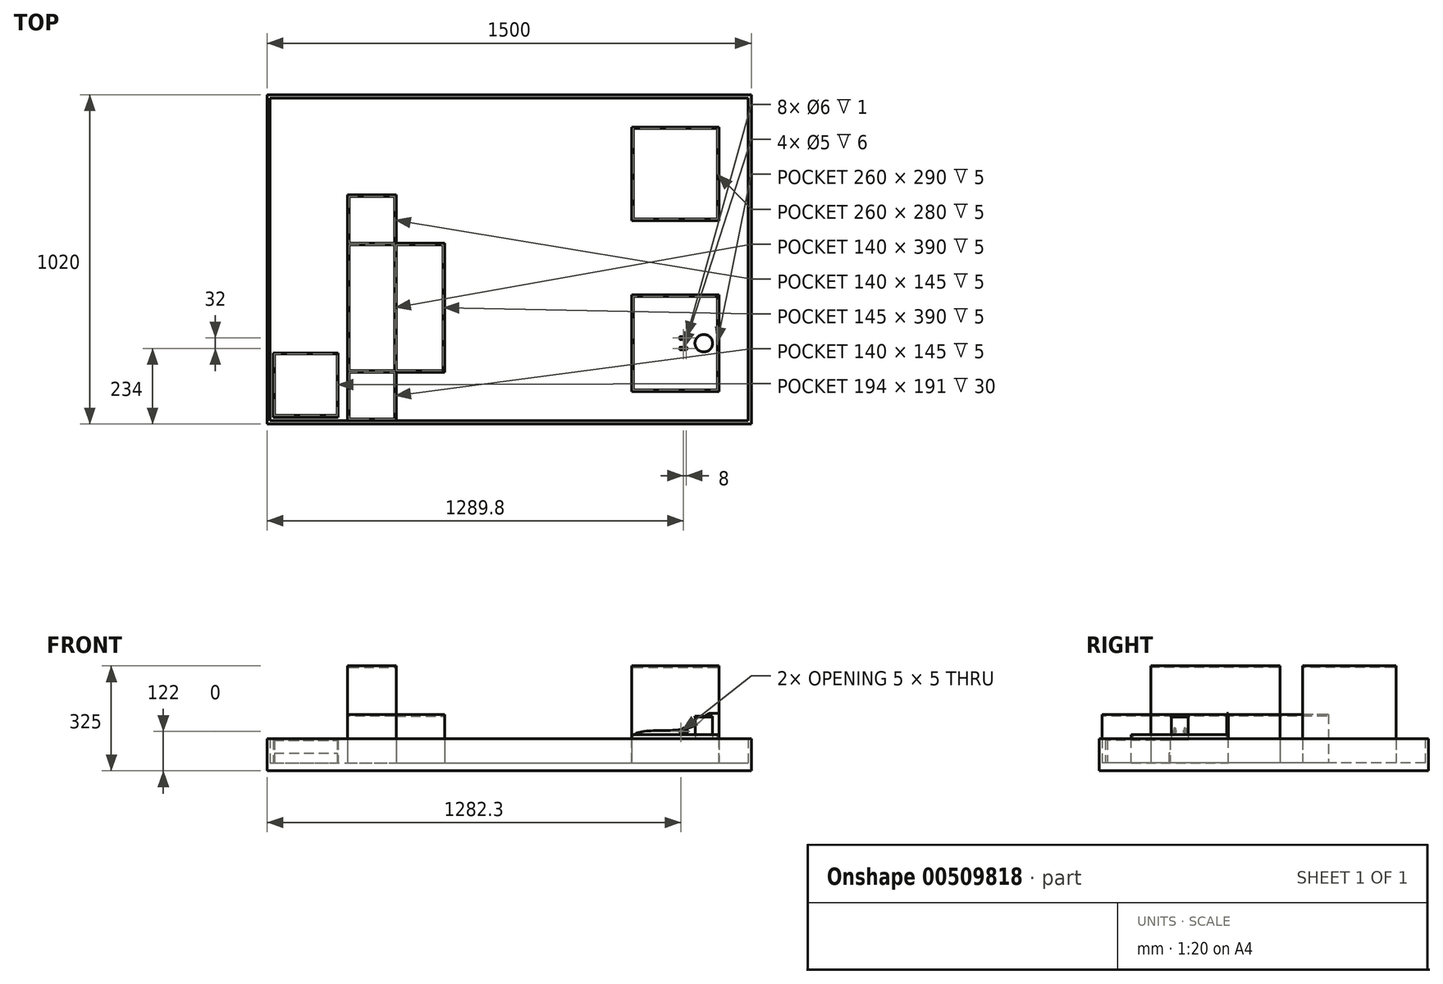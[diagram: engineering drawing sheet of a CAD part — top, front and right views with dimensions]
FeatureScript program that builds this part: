
annotation { "Feature Type Name" : "Feature", "Feature Type Description" : "" }
export const myFeature = defineFeature(function(context is Context, id is Id, definition is map)
    precondition{}
    {
        {
            var Q0;
            Q0=qCreatedBy(makeId("Top.planeOp"),FACE);
            var sketch = newSketch(context, id + "F0", { "sketchPlane" : qUnion([Q0])});
            skCircle(sketch, "E0", {"center": v(0, 0) * mm, "radius": 27.2 * mm});
            skSolve(sketch);
        }
        {
            var Q0;
            Q0=qSketchRegion(id+"F0",true);
            extrude(context, id + "F1", {"entities" : qUnion([Q0]), "depth" : 2.83 * mm});
        }
        {
            var Q0;
            Q0=makeQuery(id+"F1.opExtrude","CAP_FACE",FACE,{"disambiguationData":[OSD([sQuery(id+"F0.wireOp",EDGE,"E0")])],"isStart":false});
            var sketch = newSketch(context, id + "F2", { "sketchPlane" : qUnion([Q0])});
            skCircle(sketch, "E1", {"center": v(0, 0) * mm, "radius": 26.4 * mm});
            skSolve(sketch);
        }
        {
            var Q0;
            Q0=qSketchRegion(id+"F2",true);
            extrude(context, id + "F3", {"entities" : qUnion([Q0]), "operationType" : NewBodyOperationType.ADD, "depth" : 67.36 * mm});
        }
        {
            var Q0;
            Q0=makeQuery(id+"F3.opExtrude","CAP_FACE",FACE,{"disambiguationData":[OSD([sQuery(id+"F2.wireOp",EDGE,"E1")])],"isStart":false});
            var sketch = newSketch(context, id + "F4", { "sketchPlane" : qUnion([Q0])});
            skCircle(sketch, "E2", {"center": v(0, 0) * mm, "radius": 27.2 * mm});
            skSolve(sketch);
        }
        {
            var Q0;
            Q0=qSketchRegion(id+"F4",true);
            extrude(context, id + "F5", {"entities" : qUnion([Q0]), "operationType" : NewBodyOperationType.ADD, "depth" : 2.83 * mm});
        }
        {
            var Q0;
            Q0=makeQuery(id+"F5.opExtrude","CAP_FACE",FACE,{"disambiguationData":[OSD([sQuery(id+"F4.wireOp",EDGE,"E2")])],"isStart":false});
            var sketch = newSketch(context, id + "F6", { "sketchPlane" : qUnion([Q0])});
            skSolve(sketch);
        }
        {
            var Q0;
            Q0=qCreatedBy(makeId("Top.planeOp"),FACE);
            cPlane(context, id + "F7", {"entities" : qUnion([Q0]), "cplaneType" : CPlaneType.OFFSET, "offset" : 25 * mm, "width" : 150 * mm, "height" : 150 * mm});
        }
        {
            var Q0;
            Q0=makeQuery(id+"F6.imprint","IMPRINT",FACE,{"disambiguationData":[TD([[makeQuery(id+"F6.imprint","IMPRINT",EDGE,{"derivedFrom":makeQuery(id+"F5.opExtrude","CAP_EDGE",EDGE,{"disambiguationData":[OSD([sQuery(id+"F4.wireOp",EDGE,"E2")])],"isStart":false})}),1.0]])]});
            var sketch = newSketch(context, id + "F8", { "sketchPlane" : qUnion([Q0])});
            skSolve(sketch);
        }
        {
            var Q0;
            Q0=qCreatedBy(makeId("Top.planeOp"),FACE);
            var sketch = newSketch(context, id + "F9", { "sketchPlane" : qUnion([Q0])});
            skLineSegment(sketch, "E3.bottom", {"start": v(-222.8, -150) * mm, "end": v(47.2, -150) * mm});
            skLineSegment(sketch, "E3.top", {"start": v(-222.8, 150) * mm, "end": v(47.2, 150) * mm});
            skLineSegment(sketch, "E3.left", {"start": v(-222.8, -150) * mm, "end": v(-222.8, 150) * mm});
            skLineSegment(sketch, "E3.right", {"start": v(47.2, -150) * mm, "end": v(47.2, 150) * mm});
            skSolve(sketch);
        }
        {
            var Q0;
            Q0=qSketchRegion(id+"F9",true);
            extrude(context, id + "F10", {"entities" : qUnion([Q0]), "oppositeDirection" : true, "depth" : 72 * mm});
        }
        {
            var Q0;
            Q0=makeQuery(id+"F10.opExtrude","CAP_FACE",FACE,{"disambiguationData":[OSD([sQuery(id+"F9.wireOp",EDGE,"E3.bottom"),sQuery(id+"F9.wireOp",EDGE,"E3.top"),sQuery(id+"F9.wireOp",EDGE,"E3.left"),sQuery(id+"F9.wireOp",EDGE,"E3.right")])],"isStart":true});
            var sketch = newSketch(context, id + "F11", { "sketchPlane" : qUnion([Q0])});
            skLineSegment(sketch, "E4.bottom", {"start": v(-222.8, -150) * mm, "end": v(47.2, -150) * mm});
            skLineSegment(sketch, "E4.top", {"start": v(-222.8, -145) * mm, "end": v(42.2, -145) * mm});
            skLineSegment(sketch, "E4.left", {"start": v(-222.8, -150) * mm, "end": v(-222.8, -145) * mm});
            skLineSegment(sketch, "E5.bottom", {"start": v(47.2, 150) * mm, "end": v(42.2, 150) * mm});
            skLineSegment(sketch, "E5.left", {"start": v(47.2, 150) * mm, "end": v(47.2, -150) * mm});
            skLineSegment(sketch, "E5.right", {"start": v(42.2, 150) * mm, "end": v(42.2, -145) * mm});
            skSolve(sketch);
        }
        {
            var Q0;
            Q0=qSketchRegion(id+"F11",true);
            extrude(context, id + "F12", {"entities" : qUnion([Q0]), "operationType" : NewBodyOperationType.ADD, "depth" : 15 * mm});
        }
        {
            var Q0;
            Q0=makeQuery(id+"F12.boolean.opBoolean","MERGE",FACE,{"derivedFrom":[makeQuery(id+"F10.opExtrude","SWEPT_FACE",FACE,{"disambiguationData":[OSD([sQuery(id+"F9.wireOp",EDGE,"E3.top")])]}),makeQuery(id+"F12.opExtrude","SWEPT_FACE",FACE,{"disambiguationData":[OSD([sQuery(id+"F11.wireOp",EDGE,"E5.bottom")])]})]});
            var sketch = newSketch(context, id + "F13", { "sketchPlane" : qUnion([Q0])});
            skLineSegment(sketch, "E6", {"start": v(-47.2, 81.36) * mm, "end": v(-21.31, 81.36) * mm});
            skFitSpline(sketch, "E7", {"points": [v(-21.31, 81.36) * mm, v(15.24, 52.01) * mm, v(114.14, 28.17) * mm, v(222.8, 0) * mm], "startDerivative": vector(181.02, 0.3) * mm, "endDerivative": vector(-1.73, -239.85) * mm});
            skLineSegment(sketch, "E8", {"start": v(-47.2, 81.36) * mm, "end": v(-47.2, -72) * mm});
            skLineSegment(sketch, "E9", {"start": v(-47.2, -72) * mm, "end": v(222.8, -72) * mm});
            skLineSegment(sketch, "E10", {"start": v(222.8, -72) * mm, "end": v(222.8, 0) * mm});
            skSolve(sketch);
        }
        {
            var Q0;
            Q0=qSketchRegion(id+"F13",true);
            extrude(context, id + "F14", {"entities" : qUnion([Q0]), "operationType" : NewBodyOperationType.ADD, "oppositeDirection" : true, "depth" : 5 * mm});
        }
        {
            var Q0;
            Q0=makeQuery(id+"F10.opExtrude","CAP_FACE",FACE,{"disambiguationData":[OSD([sQuery(id+"F9.wireOp",EDGE,"E3.bottom"),sQuery(id+"F9.wireOp",EDGE,"E3.top"),sQuery(id+"F9.wireOp",EDGE,"E3.left"),sQuery(id+"F9.wireOp",EDGE,"E3.right")])],"isStart":true});
            var sketch = newSketch(context, id + "F15", { "sketchPlane" : qUnion([Q0])});
            skLineSegment(sketch, "E11.bottom", {"start": v(-222.8, 145) * mm, "end": v(-217.8, 145) * mm});
            skLineSegment(sketch, "E11.top", {"start": v(-222.8, -145) * mm, "end": v(-217.8, -145) * mm});
            skLineSegment(sketch, "E11.left", {"start": v(-222.8, 145) * mm, "end": v(-222.8, -145) * mm});
            skLineSegment(sketch, "E11.right", {"start": v(-217.8, 145) * mm, "end": v(-217.8, -145) * mm});
            skSolve(sketch);
        }
        {
            var Q0;
            Q0=qSketchRegion(id+"F15",true);
            extrude(context, id + "F16", {"entities" : qUnion([Q0]), "operationType" : NewBodyOperationType.ADD, "depth" : 5 * mm});
        }
        {
            var Q0;
            Q0=makeQuery(id+"F10.opExtrude","CAP_FACE",FACE,{"disambiguationData":[OSD([sQuery(id+"F9.wireOp",EDGE,"E3.bottom"),sQuery(id+"F9.wireOp",EDGE,"E3.top"),sQuery(id+"F9.wireOp",EDGE,"E3.left"),sQuery(id+"F9.wireOp",EDGE,"E3.right")])],"isStart":false});
            var sketch = newSketch(context, id + "F17", { "sketchPlane" : qUnion([Q0])});
            skLineSegment(sketch, "E12.bottom", {"start": v(147.2, 250) * mm, "end": v(-1352.8, 250) * mm});
            skLineSegment(sketch, "E12.top", {"start": v(147.2, -770) * mm, "end": v(-1352.8, -770) * mm});
            skLineSegment(sketch, "E12.left", {"start": v(147.2, 250) * mm, "end": v(147.2, -770) * mm});
            skLineSegment(sketch, "E12.right", {"start": v(-1352.8, 250) * mm, "end": v(-1352.8, -770) * mm});
            skSolve(sketch);
        }
        {
            var Q0;
            Q0=qSketchRegion(id+"F17",true);
            extrude(context, id + "F18", {"entities" : qUnion([Q0]), "operationType" : NewBodyOperationType.ADD, "depth" : 25 * mm});
        }
        {
            var Q0;
            Q0=makeQuery(id+"F18.opExtrude","CAP_FACE",FACE,{"disambiguationData":[OSD([sQuery(id+"F17.wireOp",EDGE,"E12.bottom"),sQuery(id+"F17.wireOp",EDGE,"E12.top"),sQuery(id+"F17.wireOp",EDGE,"E12.left"),sQuery(id+"F17.wireOp",EDGE,"E12.right")])],"isStart":true});
            var sketch = newSketch(context, id + "F19", { "sketchPlane" : qUnion([Q0])});
            skLineSegment(sketch, "E13.bottom", {"start": v(-222.8, 670) * mm, "end": v(47.2, 670) * mm});
            skLineSegment(sketch, "E13.top", {"start": v(-222.8, 380) * mm, "end": v(47.2, 380) * mm});
            skLineSegment(sketch, "E13.left", {"start": v(-222.8, 670) * mm, "end": v(-222.8, 380) * mm});
            skLineSegment(sketch, "E13.right", {"start": v(47.2, 670) * mm, "end": v(47.2, 380) * mm});
            skSolve(sketch);
        }
        {
            var Q0;
            Q0=qSketchRegion(id+"F19",true);
            extrude(context, id + "F20", {"entities" : qUnion([Q0]), "operationType" : NewBodyOperationType.ADD, "depth" : 300 * mm});
        }
        {
            var Q0;
            Q0=makeQuery(id+"F20.opExtrude","CAP_FACE",FACE,{"disambiguationData":[OSD([sQuery(id+"F19.wireOp",EDGE,"E13.bottom"),sQuery(id+"F19.wireOp",EDGE,"E13.top"),sQuery(id+"F19.wireOp",EDGE,"E13.left"),sQuery(id+"F19.wireOp",EDGE,"E13.right")])],"isStart":false});
            var sketch = newSketch(context, id + "F21", { "sketchPlane" : qUnion([Q0])});
            skLineSegment(sketch, "E14.bottom", {"start": v(-217.8, 665) * mm, "end": v(42.2, 665) * mm});
            skLineSegment(sketch, "E14.top", {"start": v(-217.8, 385) * mm, "end": v(42.2, 385) * mm});
            skLineSegment(sketch, "E14.left", {"start": v(-217.8, 665) * mm, "end": v(-217.8, 385) * mm});
            skLineSegment(sketch, "E14.right", {"start": v(42.2, 665) * mm, "end": v(42.2, 385) * mm});
            skSolve(sketch);
        }
        {
            var Q0;
            Q0=qSketchRegion(id+"F21",true);
            extrude(context, id + "F22", {"entities" : qUnion([Q0]), "operationType" : NewBodyOperationType.REMOVE, "oppositeDirection" : true, "depth" : 5 * mm});
        }
        {
            var Q0;
            Q0=makeQuery(id+"F18.opExtrude","CAP_FACE",FACE,{"disambiguationData":[OSD([sQuery(id+"F17.wireOp",EDGE,"E12.bottom"),sQuery(id+"F17.wireOp",EDGE,"E12.top"),sQuery(id+"F17.wireOp",EDGE,"E12.left"),sQuery(id+"F17.wireOp",EDGE,"E12.right")])],"isStart":true});
            var sketch = newSketch(context, id + "F23", { "sketchPlane" : qUnion([Q0])});
            skLineSegment(sketch, "E15.bottom", {"start": v(-1352.8, 770) * mm, "end": v(147.2, 770) * mm});
            skLineSegment(sketch, "E15.top", {"start": v(-1352.8, -250) * mm, "end": v(147.2, -250) * mm});
            skLineSegment(sketch, "E15.left", {"start": v(-1352.8, 770) * mm, "end": v(-1352.8, -250) * mm});
            skLineSegment(sketch, "E15.right", {"start": v(147.2, 770) * mm, "end": v(147.2, -250) * mm});
            skLineSegment(sketch, "E16.bottom", {"start": v(-1342.8, 760) * mm, "end": v(137.2, 760) * mm});
            skLineSegment(sketch, "E16.top", {"start": v(-1342.8, -240) * mm, "end": v(137.2, -240) * mm});
            skLineSegment(sketch, "E16.left", {"start": v(-1342.8, 760) * mm, "end": v(-1342.8, -240) * mm});
            skLineSegment(sketch, "E16.right", {"start": v(137.2, 760) * mm, "end": v(137.2, -240) * mm});
            skSolve(sketch);
        }
        {
            var Q0;
            Q0=qSketchRegion(id+"F23",true);
            extrude(context, id + "F24", {"entities" : qUnion([Q0]), "operationType" : NewBodyOperationType.ADD, "depth" : 75 * mm});
        }
        {
            var Q0;
            Q0=makeQuery(id+"F18.opExtrude","CAP_FACE",FACE,{"disambiguationData":[OSD([sQuery(id+"F17.wireOp",EDGE,"E12.bottom"),sQuery(id+"F17.wireOp",EDGE,"E12.top"),sQuery(id+"F17.wireOp",EDGE,"E12.left"),sQuery(id+"F17.wireOp",EDGE,"E12.right")])],"isStart":true});
            var sketch = newSketch(context, id + "F25", { "sketchPlane" : qUnion([Q0])});
            skLineSegment(sketch, "E17.bottom", {"start": v(-1102.8, 460) * mm, "end": v(-952.8, 460) * mm});
            skLineSegment(sketch, "E17.top", {"start": v(-1102.8, -240) * mm, "end": v(-952.8, -240) * mm});
            skLineSegment(sketch, "E17.left", {"start": v(-1102.8, 460) * mm, "end": v(-1102.8, -240) * mm});
            skLineSegment(sketch, "E17.right", {"start": v(-952.8, 460) * mm, "end": v(-952.8, 310) * mm});
            skLineSegment(sketch, "E18.bottom", {"start": v(-952.8, 310) * mm, "end": v(-802.8, 310) * mm});
            skLineSegment(sketch, "E18.top", {"start": v(-952.8, -90) * mm, "end": v(-802.8, -90) * mm});
            skLineSegment(sketch, "E18.right", {"start": v(-802.8, 310) * mm, "end": v(-802.8, -90) * mm});
            skLineSegment(sketch, "E19.trimOffspring", {"start": v(-952.8, -90) * mm, "end": v(-952.8, -240) * mm});
            skSolve(sketch);
        }
        {
            var Q0;
            Q0=qSketchRegion(id+"F25",true);
            extrude(context, id + "F26", {"entities" : qUnion([Q0]), "operationType" : NewBodyOperationType.ADD, "depth" : 150 * mm});
        }
        {
            var Q0;
            Q0=makeQuery(id+"F26.opExtrude","CAP_FACE",FACE,{"disambiguationData":[OSD([sQuery(id+"F25.wireOp",EDGE,"E17.bottom"),sQuery(id+"F25.wireOp",EDGE,"E17.top"),sQuery(id+"F25.wireOp",EDGE,"E17.left"),sQuery(id+"F25.wireOp",EDGE,"E17.right"),sQuery(id+"F25.wireOp",EDGE,"E18.bottom"),sQuery(id+"F25.wireOp",EDGE,"E18.top"),sQuery(id+"F25.wireOp",EDGE,"E18.right"),sQuery(id+"F25.wireOp",EDGE,"E19.trimOffspring")])],"isStart":false});
            var sketch = newSketch(context, id + "F27", { "sketchPlane" : qUnion([Q0])});
            skLineSegment(sketch, "E20.bottom", {"start": v(-952.8, 310) * mm, "end": v(-1102.8, 310) * mm});
            skLineSegment(sketch, "E20.top", {"start": v(-952.8, -90) * mm, "end": v(-1102.8, -90) * mm});
            skLineSegment(sketch, "E20.left", {"start": v(-952.8, 310) * mm, "end": v(-952.8, -90) * mm});
            skLineSegment(sketch, "E20.right", {"start": v(-1102.8, 310) * mm, "end": v(-1102.8, -90) * mm});
            skSolve(sketch);
        }
        {
            var Q0;
            Q0=qSketchRegion(id+"F27",true);
            extrude(context, id + "F28", {"entities" : qUnion([Q0]), "operationType" : NewBodyOperationType.ADD, "depth" : 150 * mm});
        }
        {
            var Q0;
            Q0=makeQuery(id+"F28.opExtrude","CAP_FACE",FACE,{"disambiguationData":[OSD([sQuery(id+"F27.wireOp",EDGE,"E20.bottom"),sQuery(id+"F27.wireOp",EDGE,"E20.top"),sQuery(id+"F27.wireOp",EDGE,"E20.left"),sQuery(id+"F27.wireOp",EDGE,"E20.right")])],"isStart":false});
            var sketch = newSketch(context, id + "F29", { "sketchPlane" : qUnion([Q0])});
            skLineSegment(sketch, "E21.bottom", {"start": v(-1097.8, 305) * mm, "end": v(-957.8, 305) * mm});
            skLineSegment(sketch, "E21.top", {"start": v(-1097.8, -85) * mm, "end": v(-957.8, -85) * mm});
            skLineSegment(sketch, "E21.left", {"start": v(-1097.8, 305) * mm, "end": v(-1097.8, -85) * mm});
            skLineSegment(sketch, "E21.right", {"start": v(-957.8, 305) * mm, "end": v(-957.8, -85) * mm});
            skSolve(sketch);
        }
        {
            var Q0;
            Q0=qSketchRegion(id+"F29",true);
            extrude(context, id + "F30", {"entities" : qUnion([Q0]), "operationType" : NewBodyOperationType.REMOVE, "oppositeDirection" : true, "depth" : 5 * mm});
        }
        {
            var Q0;
            {var subQ0=sQuery(id+"F25.wireOp",EDGE,"E17.left");var subQ1=sQuery(id+"F25.wireOp",EDGE,"E18.bottom");var subQ2=sQuery(id+"F25.wireOp",EDGE,"E17.right");var subQ3=sQuery(id+"F25.wireOp",EDGE,"E17.bottom");var subQ4=makeQuery(id+"F26.opExtrude","CAP_FACE",FACE,{"disambiguationData":[OSD([subQ3,sQuery(id+"F25.wireOp",EDGE,"E17.top"),subQ0,subQ2,subQ1,sQuery(id+"F25.wireOp",EDGE,"E18.top"),sQuery(id+"F25.wireOp",EDGE,"E18.right"),sQuery(id+"F25.wireOp",EDGE,"E19.trimOffspring")])],"isStart":false});Q0=makeQuery(id+"F28.boolean.opBoolean","SPLIT",FACE,{"disambiguationData":[TD([makeQuery(id+"F26.opExtrude","SWEPT_FACE",FACE,{"disambiguationData":[OSD([subQ3])]})])],"derivedFrom":subQ4});}
            var sketch = newSketch(context, id + "F31", { "sketchPlane" : qUnion([Q0])});
            skLineSegment(sketch, "E22.bottom", {"start": v(-1097.8, 455) * mm, "end": v(-957.8, 455) * mm});
            skLineSegment(sketch, "E22.top", {"start": v(-1097.8, 310) * mm, "end": v(-957.8, 310) * mm});
            skLineSegment(sketch, "E22.left", {"start": v(-1097.8, 455) * mm, "end": v(-1097.8, 310) * mm});
            skLineSegment(sketch, "E22.right", {"start": v(-957.8, 455) * mm, "end": v(-957.8, 310) * mm});
            skLineSegment(sketch, "E23.bottom", {"start": v(-952.8, 305) * mm, "end": v(-807.8, 305) * mm});
            skLineSegment(sketch, "E23.top", {"start": v(-952.8, -85) * mm, "end": v(-807.8, -85) * mm});
            skLineSegment(sketch, "E23.left", {"start": v(-952.8, 305) * mm, "end": v(-952.8, -85) * mm});
            skLineSegment(sketch, "E23.right", {"start": v(-807.8, 305) * mm, "end": v(-807.8, -85) * mm});
            skLineSegment(sketch, "E24.bottom", {"start": v(-1097.8, -90) * mm, "end": v(-957.8, -90) * mm});
            skLineSegment(sketch, "E24.top", {"start": v(-1097.8, -235) * mm, "end": v(-957.8, -235) * mm});
            skLineSegment(sketch, "E24.left", {"start": v(-1097.8, -90) * mm, "end": v(-1097.8, -235) * mm});
            skLineSegment(sketch, "E24.right", {"start": v(-957.8, -90) * mm, "end": v(-957.8, -235) * mm});
            skSolve(sketch);
        }
        {
            var Q0;
            Q0=qSketchRegion(id+"F31",true);
            extrude(context, id + "F32", {"entities" : qUnion([Q0]), "operationType" : NewBodyOperationType.REMOVE, "oppositeDirection" : true, "depth" : 5 * mm});
        }
        {
            var Q0;
            Q0=qCreatedBy(id+"F7.planeOp",FACE);
            var sketch = newSketch(context, id + "F33", { "sketchPlane" : qUnion([Q0])});
            skLineSegment(sketch, "E25", {"start": v(0, 0) * mm, "end": v(-90, 0) * mm, "construction": true});
            skLineSegment(sketch, "E26.bottom", {"start": v(-74.5, -12) * mm, "end": v(-55, -12) * mm});
            skLineSegment(sketch, "E26.top", {"start": v(-74.5, -20) * mm, "end": v(-55, -20) * mm});
            skLineSegment(sketch, "E26.left", {"start": v(-74.5, -12) * mm, "end": v(-74.5, -13) * mm});
            skPoint(sketch, "E27.visualSharp", {"position": v(-51, -12) * mm});
            skPoint(sketch, "E28.visualSharp", {"position": v(-51, -20) * mm});
            skCircle(sketch, "E29", {"center": v(-55, -16) * mm, "radius": 3 * mm});
            skLineSegment(sketch, "E30", {"start": v(-59, -3.98) * mm, "end": v(-59, -18.08) * mm, "construction": true});
            skCircle(sketch, "E31.MirrorC", {"center": v(-63, -16) * mm, "radius": 3 * mm});
            skLineSegment(sketch, "E32.bottom", {"start": v(-74.5, -13) * mm, "end": v(-65.65, -13) * mm});
            skLineSegment(sketch, "E32.top", {"start": v(-74.5, -19) * mm, "end": v(-65.65, -19) * mm});
            skArc(sketch, "E33", {"start": v(-65.65, -13) * mm, "mid": v(-67, -16) * mm, "end": v(-65.65, -19) * mm});
            skLineSegment(sketch, "E34.trimOffspring", {"start": v(-74.5, -19) * mm, "end": v(-74.5, -20) * mm});
            skArc(sketch, "E35.trimOffspring", {"start": v(-55, -20) * mm, "mid": v(-51, -16) * mm, "end": v(-55, -12) * mm});
            skLineSegment(sketch, "E36.MirrorCS", {"start": v(-74.5, 12) * mm, "end": v(-74.5, 13) * mm});
            skLineSegment(sketch, "E37.MirrorCS", {"start": v(-74.5, 19) * mm, "end": v(-74.5, 20) * mm});
            skPoint(sketch, "E38.MirrorP", {"position": v(-51, 12) * mm});
            skLineSegment(sketch, "E39.MirrorCS", {"start": v(-74.5, 12) * mm, "end": v(-55, 12) * mm});
            skPoint(sketch, "E40.MirrorP", {"position": v(-51, 20) * mm});
            skArc(sketch, "E41.MirrorCS", {"start": v(-65.65, 13) * mm, "mid": v(-67, 16) * mm, "end": v(-65.65, 19) * mm});
            skArc(sketch, "E42.MirrorCS", {"start": v(-55, 20) * mm, "mid": v(-51, 16) * mm, "end": v(-55, 12) * mm});
            skLineSegment(sketch, "E43.MirrorCS", {"start": v(-74.5, 20) * mm, "end": v(-55, 20) * mm});
            skCircle(sketch, "E44.MirrorC", {"center": v(-55, 16) * mm, "radius": 3 * mm});
            skCircle(sketch, "E45.MirrorC", {"center": v(-63, 16) * mm, "radius": 3 * mm});
            skLineSegment(sketch, "E46.MirrorCS", {"start": v(-74.5, 19) * mm, "end": v(-65.65, 19) * mm});
            skLineSegment(sketch, "E47.MirrorCS", {"start": v(-74.5, 13) * mm, "end": v(-65.65, 13) * mm});
            skSolve(sketch);
        }
        {
            var Q0;
            Q0=qSketchRegion(id+"F33",true);
            var Q1;
            Q1=qSketchRegion(id+"F36",true);
            extrude(context, id + "F34", {"entities" : qUnion([Q0, Q1]), "endBound" : BoundingType.SYMMETRIC, "depth" : 8 * mm});
        }
        {
            var Q0;
            Q0=makeQuery(id+"F34.opExtrude","CAP_EDGE",EDGE,{"disambiguationData":[OSD([sQuery(id+"F33.wireOp",EDGE,"E34.trimOffspring")])],"isStart":false});
            var Q1;
            Q1=makeQuery(id+"F34.opExtrude","CAP_EDGE",EDGE,{"disambiguationData":[OSD([sQuery(id+"F33.wireOp",EDGE,"E26.left")])],"isStart":false});
            var Q2;
            Q2=makeQuery(id+"F34.opExtrude","CAP_EDGE",EDGE,{"disambiguationData":[OSD([sQuery(id+"F33.wireOp",EDGE,"E34.trimOffspring")])],"isStart":true});
            var Q3;
            Q3=makeQuery(id+"F34.opExtrude","CAP_EDGE",EDGE,{"disambiguationData":[OSD([sQuery(id+"F33.wireOp",EDGE,"E26.left")])],"isStart":true});
            var Q4;
            Q4=makeQuery(id+"F34.opExtrude","CAP_EDGE",EDGE,{"disambiguationData":[OSD([sQuery(id+"F33.wireOp",EDGE,"E36.MirrorCS")])],"isStart":false});
            var Q5;
            Q5=makeQuery(id+"F34.opExtrude","CAP_EDGE",EDGE,{"disambiguationData":[OSD([sQuery(id+"F33.wireOp",EDGE,"E37.MirrorCS")])],"isStart":false});
            var Q6;
            Q6=makeQuery(id+"F34.opExtrude","CAP_EDGE",EDGE,{"disambiguationData":[OSD([sQuery(id+"F33.wireOp",EDGE,"E37.MirrorCS")])],"isStart":true});
            var Q7;
            Q7=makeQuery(id+"F34.opExtrude","CAP_EDGE",EDGE,{"disambiguationData":[OSD([sQuery(id+"F33.wireOp",EDGE,"E36.MirrorCS")])],"isStart":true});
            fillet(context, id + "F35", {"entities" : qUnion([Q0, Q1, Q2, Q3, Q4, Q5, Q6, Q7]), "radius" : 4 * mm, "tangentPropagation" : true, "allowEdgeOverflow" : false});
        }
        {
            var Q0;
            Q0=makeQuery(id+"F34.opExtrude","SWEPT_FACE",FACE,{"disambiguationData":[OSD([sQuery(id+"F33.wireOp",EDGE,"E26.top")])]});
            var sketch = newSketch(context, id + "F36", { "sketchPlane" : qUnion([Q0])});
            skCircle(sketch, "E48", {"center": v(-70.5, 25) * mm, "radius": 3 * mm});
            skSolve(sketch);
        }
        {
            var Q0;
            Q0=qSketchRegion(id+"F36",true);
            var Q1;
            Q1=makeQuery(id+"F34.opExtrude","SWEPT_FACE",FACE,{"disambiguationData":[OSD([sQuery(id+"F33.wireOp",EDGE,"E26.bottom")])]});
            extrude(context, id + "F37", {"entities" : qUnion([Q0]), "operationType" : NewBodyOperationType.ADD, "endBound" : BoundingType.UP_TO_SURFACE, "oppositeDirection" : true, "endBoundEntityFace" : qUnion([Q1]), "depth" : 25 * mm});
        }
        {
            var Q0;
            Q0=makeQuery(id+"F34.opExtrude","SWEPT_FACE",FACE,{"disambiguationData":[OSD([sQuery(id+"F33.wireOp",EDGE,"E43.MirrorCS")])]});
            var sketch = newSketch(context, id + "F38", { "sketchPlane" : qUnion([Q0])});
            skCircle(sketch, "E49", {"center": v(70.5, 25) * mm, "radius": 3 * mm});
            skSolve(sketch);
        }
        {
            var Q0;
            Q0=qSketchRegion(id+"F38",true);
            var Q1;
            Q1=makeQuery(id+"F34.opExtrude","SWEPT_FACE",FACE,{"disambiguationData":[OSD([sQuery(id+"F33.wireOp",EDGE,"E39.MirrorCS")])]});
            extrude(context, id + "F39", {"entities" : qUnion([Q0]), "operationType" : NewBodyOperationType.ADD, "endBound" : BoundingType.UP_TO_SURFACE, "oppositeDirection" : true, "endBoundEntityFace" : qUnion([Q1]), "depth" : 25 * mm});
        }
        {
            var Q0;
            Q0=qCreatedBy(id+"F7.planeOp",FACE);
            var sketch = newSketch(context, id + "F40", { "sketchPlane" : qUnion([Q0])});
            skCircle(sketch, "E50", {"center": v(-55, 16) * mm, "radius": 3 * mm});
            skCircle(sketch, "E51", {"center": v(-63, 16) * mm, "radius": 2.5 * mm});
            skCircle(sketch, "E52", {"center": v(-63, 16) * mm, "radius": 3 * mm});
            skCircle(sketch, "E53", {"center": v(-55, 16) * mm, "radius": 2.5 * mm});
            skSolve(sketch);
        }
        {
            var Q0;
            Q0=qSketchRegion(id+"F40",true);
            extrude(context, id + "F41", {"entities" : qUnion([Q0]), "operationType" : NewBodyOperationType.ADD, "endBound" : BoundingType.SYMMETRIC, "depth" : 6 * mm});
        }
        {
            var Q0;
            Q0=qCreatedBy(id+"F7.planeOp",FACE);
            var sketch = newSketch(context, id + "F42", { "sketchPlane" : qUnion([Q0])});
            skCircle(sketch, "E54", {"center": v(-63, -16) * mm, "radius": 2.5 * mm});
            skCircle(sketch, "E55", {"center": v(-63, -16) * mm, "radius": 3 * mm});
            skCircle(sketch, "E56", {"center": v(-55, -16) * mm, "radius": 2.5 * mm});
            skCircle(sketch, "E57", {"center": v(-55, -16) * mm, "radius": 3 * mm});
            skSolve(sketch);
        }
        {
            var Q0;
            Q0=qSketchRegion(id+"F42",true);
            extrude(context, id + "F43", {"entities" : qUnion([Q0]), "operationType" : NewBodyOperationType.ADD, "endBound" : BoundingType.SYMMETRIC, "depth" : 6 * mm});
        }
        {
            var Q0;
            Q0=makeQuery(id+"F34.opExtrude","SWEPT_FACE",FACE,{"disambiguationData":[OSD([sQuery(id+"F33.wireOp",EDGE,"E43.MirrorCS")])]});
            var sketch = newSketch(context, id + "F44", { "sketchPlane" : qUnion([Q0])});
            skArc(sketch, "E58", {"start": v(71.5, 27.3) * mm, "mid": v(70.5, 27.5) * mm, "end": v(69.5, 27.3) * mm});
            skLineSegment(sketch, "E59.bottom", {"start": v(68.2, 26) * mm, "end": v(69.5, 26) * mm});
            skLineSegment(sketch, "E59.top", {"start": v(68.2, 24) * mm, "end": v(69.5, 24) * mm});
            skLineSegment(sketch, "E60.left", {"start": v(71.5, 27.3) * mm, "end": v(71.5, 26) * mm});
            skLineSegment(sketch, "E60.right", {"start": v(69.5, 27.3) * mm, "end": v(69.5, 26) * mm});
            skPoint(sketch, "E61.orphan", {"position": v(69.5, 27.8) * mm});
            skPoint(sketch, "E62.orphan", {"position": v(71.5, 27.8) * mm});
            skArc(sketch, "E63.trimOffspring", {"start": v(68.2, 26) * mm, "mid": v(68, 25) * mm, "end": v(68.2, 24) * mm});
            skPoint(sketch, "E59.left.start.orphan", {"position": v(67.32, 26) * mm});
            skPoint(sketch, "E64.orphan", {"position": v(67.32, 24) * mm});
            skArc(sketch, "E65.trimOffspring", {"start": v(69.5, 22.7) * mm, "mid": v(70.5, 22.5) * mm, "end": v(71.5, 22.7) * mm});
            skLineSegment(sketch, "E66.trimOffspring", {"start": v(69.5, 24) * mm, "end": v(69.5, 22.7) * mm});
            skLineSegment(sketch, "E67.trimOffspring", {"start": v(71.5, 26) * mm, "end": v(72.8, 26) * mm});
            skLineSegment(sketch, "E68.trimOffspring", {"start": v(71.5, 24) * mm, "end": v(71.5, 22.7) * mm});
            skLineSegment(sketch, "E69.trimOffspring", {"start": v(71.5, 24) * mm, "end": v(72.8, 24) * mm});
            skPoint(sketch, "E60.top.end.orphan", {"position": v(69.5, 22.2) * mm});
            skPoint(sketch, "E70.orphan", {"position": v(71.5, 22.2) * mm});
            skPoint(sketch, "E59.right.end.orphan", {"position": v(73.68, 24) * mm});
            skPoint(sketch, "E71.orphan", {"position": v(73.68, 26) * mm});
            skArc(sketch, "E72.trimOffspring", {"start": v(72.8, 24) * mm, "mid": v(73, 25) * mm, "end": v(72.8, 26) * mm});
            skSolve(sketch);
        }
        {
            var Q0;
            Q0=qSketchRegion(id+"F44",true);
            extrude(context, id + "F45", {"entities" : qUnion([Q0]), "operationType" : NewBodyOperationType.REMOVE, "endBound" : BoundingType.THROUGH_ALL, "oppositeDirection" : true, "depth" : 25 * mm});
        }
        {
            var Q0;
            Q0=makeQuery(id+"F18.opExtrude","CAP_FACE",FACE,{"disambiguationData":[OSD([sQuery(id+"F17.wireOp",EDGE,"E12.bottom"),sQuery(id+"F17.wireOp",EDGE,"E12.top"),sQuery(id+"F17.wireOp",EDGE,"E12.left"),sQuery(id+"F17.wireOp",EDGE,"E12.right")])],"isStart":true});
            var sketch = newSketch(context, id + "F46", { "sketchPlane" : qUnion([Q0])});
            skLineSegment(sketch, "E73.bottom", {"start": v(-1332.8, -30) * mm, "end": v(-1132.8, -30) * mm});
            skLineSegment(sketch, "E73.top", {"start": v(-1332.8, -230) * mm, "end": v(-1132.8, -230) * mm});
            skLineSegment(sketch, "E73.left", {"start": v(-1332.8, -30) * mm, "end": v(-1332.8, -230) * mm});
            skLineSegment(sketch, "E73.right", {"start": v(-1132.8, -30) * mm, "end": v(-1132.8, -230) * mm});
            skLineSegment(sketch, "E74.bottom", {"start": v(-1329.8, -33) * mm, "end": v(-1135.8, -33) * mm});
            skLineSegment(sketch, "E74.top", {"start": v(-1329.8, -224) * mm, "end": v(-1135.8, -224) * mm});
            skLineSegment(sketch, "E74.left", {"start": v(-1329.8, -33) * mm, "end": v(-1329.8, -224) * mm});
            skLineSegment(sketch, "E74.right", {"start": v(-1135.8, -33) * mm, "end": v(-1135.8, -224) * mm});
            skSolve(sketch);
        }
        {
            var Q0;
            Q0=qSketchRegion(id+"F46",true);
            extrude(context, id + "F47", {"entities" : qUnion([Q0]), "operationType" : NewBodyOperationType.ADD, "depth" : 30 * mm});
        }
        {
            var Q0;
            Q0=makeQuery(id+"F47.opExtrude","CAP_FACE",FACE,{"disambiguationData":[OSD([sQuery(id+"F46.wireOp",EDGE,"E73.bottom"),sQuery(id+"F46.wireOp",EDGE,"E73.top"),sQuery(id+"F46.wireOp",EDGE,"E73.left"),sQuery(id+"F46.wireOp",EDGE,"E73.right"),sQuery(id+"F46.wireOp",EDGE,"E74.bottom"),sQuery(id+"F46.wireOp",EDGE,"E74.top"),sQuery(id+"F46.wireOp",EDGE,"E74.left"),sQuery(id+"F46.wireOp",EDGE,"E74.right")])],"isStart":false});
            var sketch = newSketch(context, id + "F48", { "sketchPlane" : qUnion([Q0])});
            skLineSegment(sketch, "E75.bottom", {"start": v(-1332.8, -30) * mm, "end": v(-1329.8, -30) * mm});
            skLineSegment(sketch, "E75.top", {"start": v(-1332.8, -230) * mm, "end": v(-1329.8, -230) * mm});
            skLineSegment(sketch, "E75.left", {"start": v(-1332.8, -30) * mm, "end": v(-1332.8, -230) * mm});
            skLineSegment(sketch, "E75.right", {"start": v(-1329.8, -30) * mm, "end": v(-1329.8, -224) * mm});
            skLineSegment(sketch, "E76.bottom", {"start": v(-1329.8, -230) * mm, "end": v(-1135.8, -230) * mm});
            skLineSegment(sketch, "E76.top", {"start": v(-1329.8, -224) * mm, "end": v(-1135.8, -224) * mm});
            skLineSegment(sketch, "E77.bottom", {"start": v(-1135.8, -230) * mm, "end": v(-1132.8, -230) * mm});
            skLineSegment(sketch, "E77.top", {"start": v(-1135.8, -30) * mm, "end": v(-1132.8, -30) * mm});
            skLineSegment(sketch, "E77.left", {"start": v(-1135.8, -224) * mm, "end": v(-1135.8, -30) * mm});
            skLineSegment(sketch, "E77.right", {"start": v(-1132.8, -230) * mm, "end": v(-1132.8, -30) * mm});
            skSolve(sketch);
        }
        {
            var Q0;
            Q0=qSketchRegion(id+"F48",true);
            extrude(context, id + "F49", {"entities" : qUnion([Q0]), "operationType" : NewBodyOperationType.ADD, "depth" : 40 * mm});
        }
        {
            var Q0;
            Q0=makeQuery(id+"F34.opExtrude","CAP_FACE",FACE,{"disambiguationData":[OSD([sQuery(id+"F33.wireOp",EDGE,"E36.MirrorCS"),sQuery(id+"F33.wireOp",EDGE,"E37.MirrorCS"),sQuery(id+"F33.wireOp",EDGE,"E39.MirrorCS"),sQuery(id+"F33.wireOp",EDGE,"E41.MirrorCS"),sQuery(id+"F33.wireOp",EDGE,"E42.MirrorCS"),sQuery(id+"F33.wireOp",EDGE,"E43.MirrorCS"),sQuery(id+"F33.wireOp",EDGE,"E44.MirrorC"),sQuery(id+"F33.wireOp",EDGE,"E45.MirrorC"),sQuery(id+"F33.wireOp",EDGE,"E46.MirrorCS"),sQuery(id+"F33.wireOp",EDGE,"E47.MirrorCS")])],"isStart":false});
            var sketch = newSketch(context, id + "F50", { "sketchPlane" : qUnion([Q0])});
            skLineSegment(sketch, "E78", {"start": v(-74.3, -20.27) * mm, "end": v(-37.61, -20.27) * mm});
            skLineSegment(sketch, "E79", {"start": v(-74.54, -11.95) * mm, "end": v(-37.61, -7.24) * mm});
            skArc(sketch, "E80", {"start": v(-37.61, -20.27) * mm, "mid": v(-10.47, -45.9) * mm, "end": v(23.27, -29.9) * mm});
            skPoint(sketch, "E81", {"position": v(-74.08, 19.82) * mm});
            skPoint(sketch, "E82", {"position": v(-74.08, 11.5) * mm});
            skLineSegment(sketch, "E83", {"start": v(-74.54, -20.27) * mm, "end": v(-74.54, -11.95) * mm});
            skLineSegment(sketch, "E84", {"start": v(-74.08, 19.82) * mm, "end": v(-74.08, 11.5) * mm});
            skLineSegment(sketch, "E85", {"start": v(-74.08, 19.82) * mm, "end": v(-37.61, 19.98) * mm});
            skLineSegment(sketch, "E86", {"start": v(-74.08, 11.5) * mm, "end": v(-37.61, 5.82) * mm});
            skArc(sketch, "E87", {"start": v(-37.61, -7.24) * mm, "mid": v(-33.13, -0.7) * mm, "end": v(-37.61, 5.82) * mm});
            skArc(sketch, "E88", {"start": v(23.27, 30.24) * mm, "mid": v(-10.75, 46.4) * mm, "end": v(-37.61, 19.98) * mm});
            skLineSegment(sketch, "E89", {"start": v(23.27, 30.24) * mm, "end": v(23.27, 26.24) * mm});
            skLineSegment(sketch, "E90", {"start": v(23.27, -29.9) * mm, "end": v(23.27, -25.9) * mm});
            skArc(sketch, "E91", {"start": v(23.27, 26.24) * mm, "mid": v(-28.05, 0.17) * mm, "end": v(23.27, -25.9) * mm});
            skCircle(sketch, "E92", {"center": v(-63, 16) * mm, "radius": 2.54 * mm});
            skCircle(sketch, "E93", {"center": v(-55, 16) * mm, "radius": 2.63 * mm});
            skCircle(sketch, "E94", {"center": v(-55, -16) * mm, "radius": 2.46 * mm});
            skCircle(sketch, "E95", {"center": v(-63, -16) * mm, "radius": 2.46 * mm});
            skSolve(sketch);
        }
        {
            var Q0;
            Q0=qSketchRegion(id+"F50",true);
            extrude(context, id + "F51", {"entities" : qUnion([Q0]), "depth" : 6 * mm});
        }
    });
